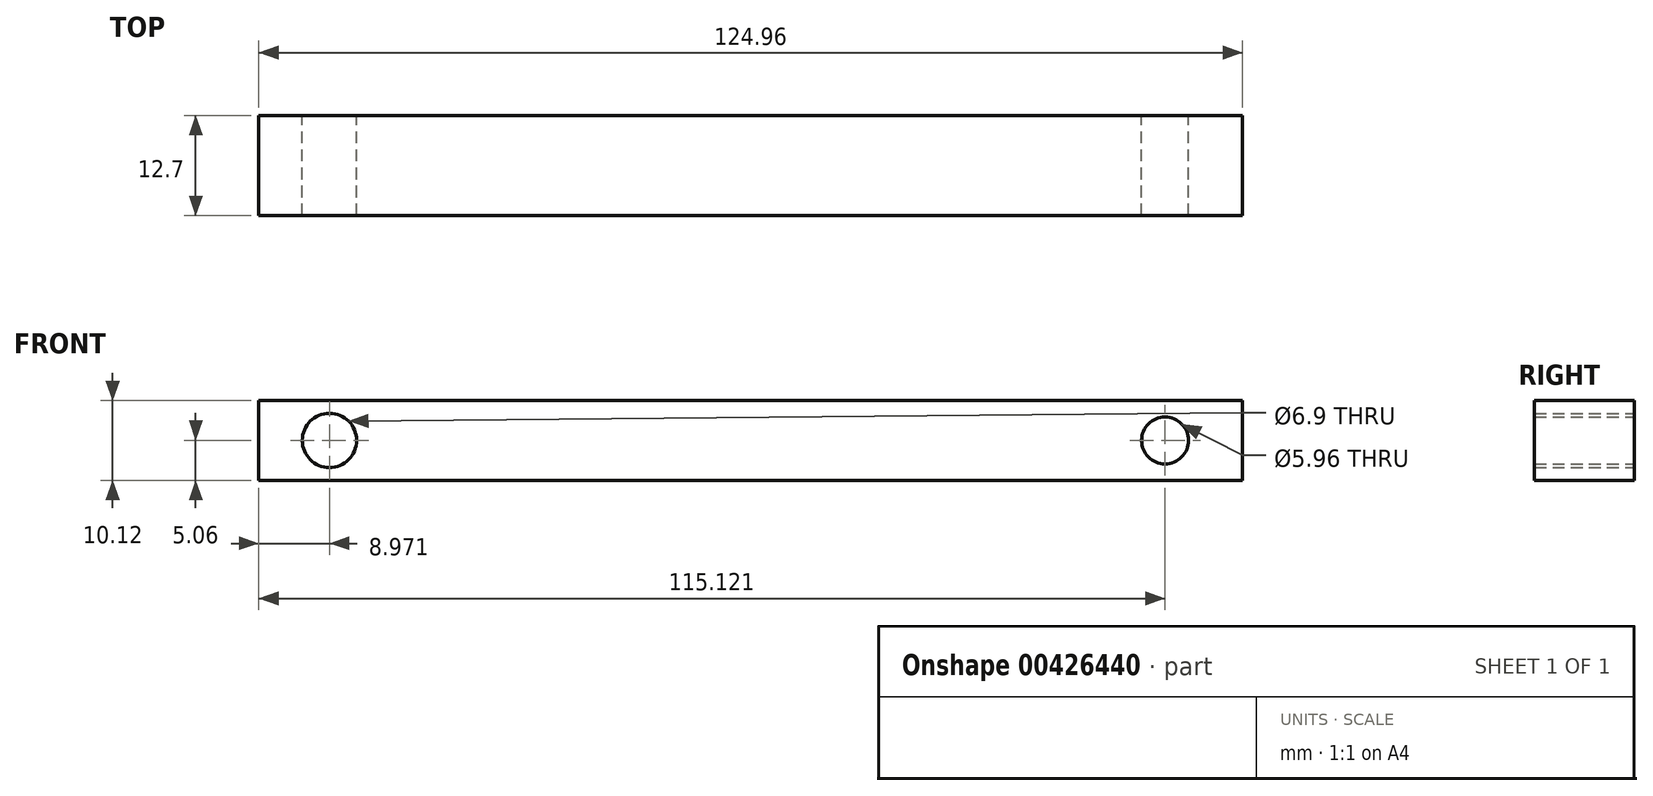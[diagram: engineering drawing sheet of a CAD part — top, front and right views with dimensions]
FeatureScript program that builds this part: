
annotation { "Feature Type Name" : "Feature", "Feature Type Description" : "" }
export const myFeature = defineFeature(function(context is Context, id is Id, definition is map)
    precondition{}
    {
        {
            var Q0;
            Q0=qCreatedBy(makeId("Front.planeOp"),FACE);
            var sketch = newSketch(context, id + "F0", { "sketchPlane" : qUnion([Q0])});
            skLineSegment(sketch, "E0.bottom", {"start": v(-62.48, 5.06) * mm, "end": v(62.48, 5.06) * mm});
            skLineSegment(sketch, "E0.top", {"start": v(-62.48, -5.06) * mm, "end": v(62.48, -5.06) * mm});
            skLineSegment(sketch, "E0.left", {"start": v(-62.48, 5.06) * mm, "end": v(-62.48, -5.06) * mm});
            skLineSegment(sketch, "E0.right", {"start": v(62.48, 5.06) * mm, "end": v(62.48, -5.06) * mm});
            skPoint(sketch, "E0.middle", {"position": v(0, 0) * mm});
            skCircle(sketch, "E1", {"center": v(-53.5, 0) * mm, "radius": 3.45 * mm});
            skCircle(sketch, "E2", {"center": v(52.64, 0) * mm, "radius": 2.98 * mm});
            skSolve(sketch);
        }
        {
            var Q0;
            Q0=makeQuery(id+"F0.imprint","IMPRINT",FACE,{"disambiguationData":[TD([[makeQuery(id+"F0.imprint","IMPRINT",EDGE,{"derivedFrom":sQuery(id+"F0.wireOp",EDGE,"E0.bottom")}),-1.0]])]});
            extrude(context, id + "F1", {"entities" : qUnion([Q0]), "endBound" : BoundingType.SYMMETRIC, "depth" : 12.7 * mm});
        }
    });
